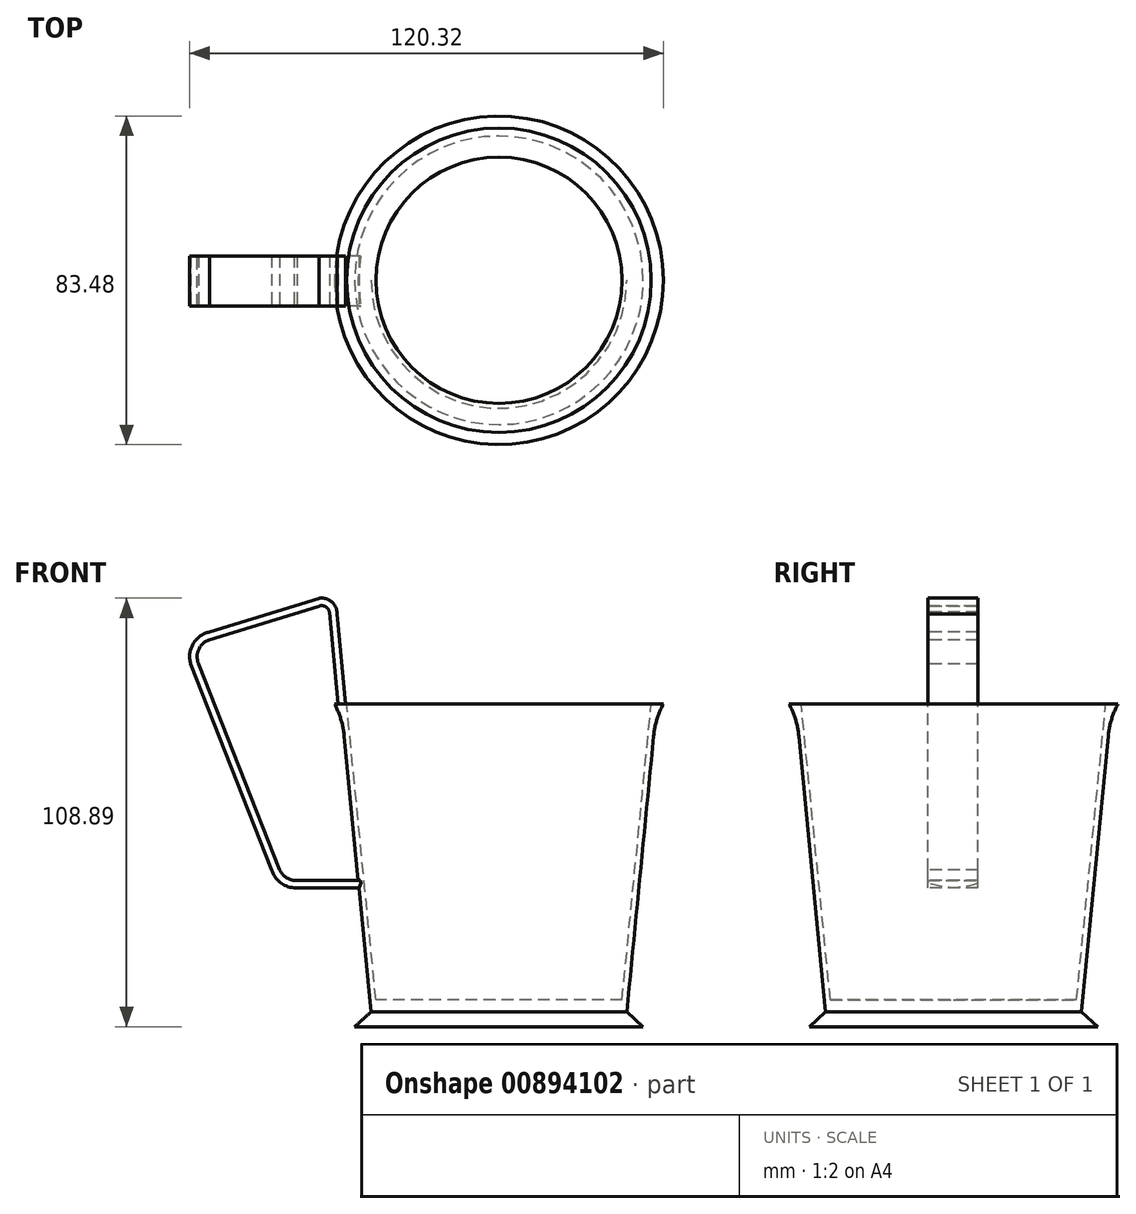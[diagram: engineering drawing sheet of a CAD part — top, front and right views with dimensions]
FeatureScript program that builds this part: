
annotation { "Feature Type Name" : "Feature", "Feature Type Description" : "" }
export const myFeature = defineFeature(function(context is Context, id is Id, definition is map)
    precondition{}
    {
        {
            var Q0;
            Q0=qCreatedBy(makeId("Top.planeOp"),FACE);
            var sketch = newSketch(context, id + "F0", { "sketchPlane" : qUnion([Q0])});
            skCircle(sketch, "E0", {"center": v(0, 0) * mm, "radius": 33.02 * mm});
            skSolve(sketch);
        }
        {
            var Q0;
            Q0=makeQuery(id+"F0.imprint","IMPRINT",FACE,{"disambiguationData":[TD([[makeQuery(id+"F0.imprint","IMPRINT",EDGE,{"derivedFrom":sQuery(id+"F0.wireOp",EDGE,"E0")}),1.0]])]});
            extrude(context, id + "F1", {"entities" : qUnion([Q0]), "depth" : 78.23 * mm, "offsetDistance" : 25.4 * mm, "hasDraft" : true, "draftAngle" : 5.63 * degree});
        }
        {
            var Q0;
            Q0=qCreatedBy(makeId("Front.planeOp"),FACE);
            var sketch = newSketch(context, id + "F2", { "sketchPlane" : qUnion([Q0])});
            skLineSegment(sketch, "E1", {"start": v(0, 0) * mm, "end": v(-32.51, 0) * mm});
            skLineSegment(sketch, "E2", {"start": v(-36.65, -3.7) * mm, "end": v(0, -3.7) * mm});
            skLineSegment(sketch, "E3", {"start": v(0, -3.7) * mm, "end": v(0, 0) * mm});
            skLineSegment(sketch, "E4", {"start": v(-32.51, 0) * mm, "end": v(-36.65, -3.7) * mm});
            skSolve(sketch);
        }
        {
            var Q0;
            Q0=makeQuery(id+"F1.opExtrude","CAP_FACE",FACE,{"disambiguationData":[OSD([sQuery(id+"F0.wireOp",EDGE,"E0")])],"isStart":true});
            var sketch = newSketch(context, id + "F3", { "sketchPlane" : qUnion([Q0])});
            skCircle(sketch, "E5", {"center": v(0, 0) * mm, "radius": 34.04 * mm});
            skSolve(sketch);
        }
        {
            var Q0;
            Q0=makeQuery(id+"F3.imprint","IMPRINT",FACE,{"disambiguationData":[TD([[makeQuery(id+"F3.imprint","IMPRINT",EDGE,{"derivedFrom":sQuery(id+"F3.wireOp",EDGE,"E5")}),1.0]])]});
            extrude(context, id + "F4", {"entities" : qUnion([Q0]), "operationType" : NewBodyOperationType.ADD, "oppositeDirection" : true, "depth" : 78.23 * mm, "offsetDistance" : 25.4 * mm, "hasDraft" : true, "draftAngle" : 5.63 * degree});
        }
        {
            var Q0;
            {var subQ0=sQuery(id+"F0.wireOp",EDGE,"E0");Q0=makeQuery(id+"F4.boolean.opBoolean","MERGE",FACE,{"derivedFrom":[makeQuery(id+"F1.opExtrude","CAP_FACE",FACE,{"disambiguationData":[OSD([subQ0])],"isStart":false}),makeQuery(id+"F4.opExtrude","CAP_FACE",FACE,{"disambiguationData":[OSD([subQ0,sQuery(id+"F3.wireOp",EDGE,"E5")])],"isStart":false})]});}
            shell(context, id + "F5", {"entities" : qUnion([Q0]), "thickness" : 3.05 * mm});
        }
        {
            var Q0;
            Q0=qCreatedBy(makeId("Front.planeOp"),FACE);
            var sketch = newSketch(context, id + "F6", { "sketchPlane" : qUnion([Q0])});
            skLineSegment(sketch, "E6", {"start": v(32.5, 0) * mm, "end": v(39.3, 70.15) * mm});
            skArc(sketch, "E7", {"start": v(41.78, 78.3) * mm, "mid": v(40.13, 74.35) * mm, "end": v(39.3, 70.15) * mm});
            skLineSegment(sketch, "E8", {"start": v(41.78, 78.3) * mm, "end": v(50.5, 78.3) * mm});
            skLineSegment(sketch, "E9", {"start": v(50.5, 78.3) * mm, "end": v(50.5, 0) * mm});
            skLineSegment(sketch, "E10", {"start": v(50.5, 0) * mm, "end": v(32.5, 0) * mm});
            skLineSegment(sketch, "E11", {"start": v(0, 0) * mm, "end": v(0, 77.76) * mm});
            skSolve(sketch);
        }
        {
            var Q0;
            Q0=makeQuery(id+"F6.imprint","IMPRINT",FACE,{"disambiguationData":[TD([[makeQuery(id+"F6.imprint","IMPRINT",EDGE,{"derivedFrom":sQuery(id+"F6.wireOp",EDGE,"E6")}),-1.0]])]});
            var Q1;
            Q1=sQuery(id+"F6.wireOp",EDGE,"E11");
            revolve(context, id + "F7", {"operationType" : NewBodyOperationType.REMOVE, "surfaceOperationType" : NewSurfaceOperationType.NEW, "entities" : qUnion([Q0]), "axis" : qUnion([Q1]), "revolveType" : RevolveType.FULL, "oppositeDirection" : true});
        }
        {
            var Q0;
            Q0=qCreatedBy(makeId("Front.planeOp"),FACE);
            var sketch = newSketch(context, id + "F8", { "sketchPlane" : qUnion([Q0])});
            skLineSegment(sketch, "E12", {"start": v(-40.28, 77.82) * mm, "end": v(-42.5, 101.52) * mm});
            skLineSegment(sketch, "E13", {"start": v(-45.78, 103.7) * mm, "end": v(-73.64, 95.15) * mm});
            skLineSegment(sketch, "E14", {"start": v(-76.88, 88.43) * mm, "end": v(-56.29, 36.1) * mm});
            skLineSegment(sketch, "E15", {"start": v(-51.56, 32.88) * mm, "end": v(-35.06, 32.88) * mm});
            skPoint(sketch, "E16.visualSharp", {"position": v(-40.94, 105.2) * mm});
            skArc(sketch, "E16.filletArc", {"start": v(-42.5, 101.52) * mm, "mid": v(-43.63, 103.39) * mm, "end": v(-45.78, 103.7) * mm});
            skPoint(sketch, "E17.visualSharp", {"position": v(-78.89, 93.53) * mm});
            skArc(sketch, "E17.filletArc", {"start": v(-73.64, 95.15) * mm, "mid": v(-76.73, 92.5) * mm, "end": v(-76.88, 88.43) * mm});
            skPoint(sketch, "E18.visualSharp", {"position": v(-55.02, 32.88) * mm});
            skArc(sketch, "E18.filletArc", {"start": v(-56.29, 36.1) * mm, "mid": v(-54.42, 33.76) * mm, "end": v(-51.56, 32.88) * mm});
            skSolve(sketch);
        }
        {
            var Q0;
            {var subQ0=sQuery(id+"F0.wireOp",EDGE,"E0");Q0=makeQuery(id+"F4.boolean.opBoolean","MERGE",FACE,{"derivedFrom":[makeQuery(id+"F1.opExtrude","CAP_FACE",FACE,{"disambiguationData":[OSD([subQ0])],"isStart":false}),makeQuery(id+"F4.opExtrude","CAP_FACE",FACE,{"disambiguationData":[OSD([subQ0,sQuery(id+"F3.wireOp",EDGE,"E5")])],"isStart":false})]});}
            var sketch = newSketch(context, id + "F9", { "sketchPlane" : qUnion([Q0])});
            skLineSegment(sketch, "E19.bottom", {"start": v(-74.3, 6.2) * mm, "end": v(-72.26, 6.2) * mm});
            skLineSegment(sketch, "E19.top", {"start": v(-74.3, -6.5) * mm, "end": v(-72.26, -6.5) * mm});
            skLineSegment(sketch, "E19.left", {"start": v(-74.3, 6.2) * mm, "end": v(-74.3, -6.5) * mm});
            skLineSegment(sketch, "E19.right", {"start": v(-72.26, 6.2) * mm, "end": v(-72.26, -6.5) * mm});
            skSolve(sketch);
        }
        {
            var Q0;
            Q0=makeQuery(id+"F9.imprint","IMPRINT",FACE,{"disambiguationData":[TD([[makeQuery(id+"F9.imprint","IMPRINT",EDGE,{"derivedFrom":sQuery(id+"F9.wireOp",EDGE,"E19.bottom")}),-1.0]])]});
            var Q1;
            Q1=sQuery(id+"F8.wireOp",EDGE,"E14");
            var Q2;
            Q2=sQuery(id+"F8.wireOp",EDGE,"E17.filletArc");
            var Q3;
            Q3=sQuery(id+"F8.wireOp",EDGE,"E13");
            var Q4;
            Q4=sQuery(id+"F8.wireOp",EDGE,"E16.filletArc");
            var Q5;
            Q5=sQuery(id+"F8.wireOp",EDGE,"E12");
            var Q6;
            Q6=sQuery(id+"F8.wireOp",EDGE,"E18.filletArc");
            var Q7;
            Q7=sQuery(id+"F8.wireOp",EDGE,"E15");
            sweep(context, id + "F10", {"operationType" : NewBodyOperationType.ADD, "profiles" : qUnion([Q0]), "path" : qUnion([Q1, Q2, Q3, Q4, Q5, Q6, Q7])});
        }
        {
            var Q0;
            Q0=makeQuery(id+"F2.imprint","IMPRINT",FACE,{"disambiguationData":[TD([[makeQuery(id+"F2.imprint","IMPRINT",EDGE,{"derivedFrom":sQuery(id+"F2.wireOp",EDGE,"E1")}),1.0]])]});
            var Q1;
            Q1=sQuery(id+"F2.wireOp",EDGE,"E3");
            revolve(context, id + "F11", {"operationType" : NewBodyOperationType.ADD, "surfaceOperationType" : NewSurfaceOperationType.NEW, "entities" : qUnion([Q0]), "axis" : qUnion([Q1]), "revolveType" : RevolveType.FULL});
        }
    });
